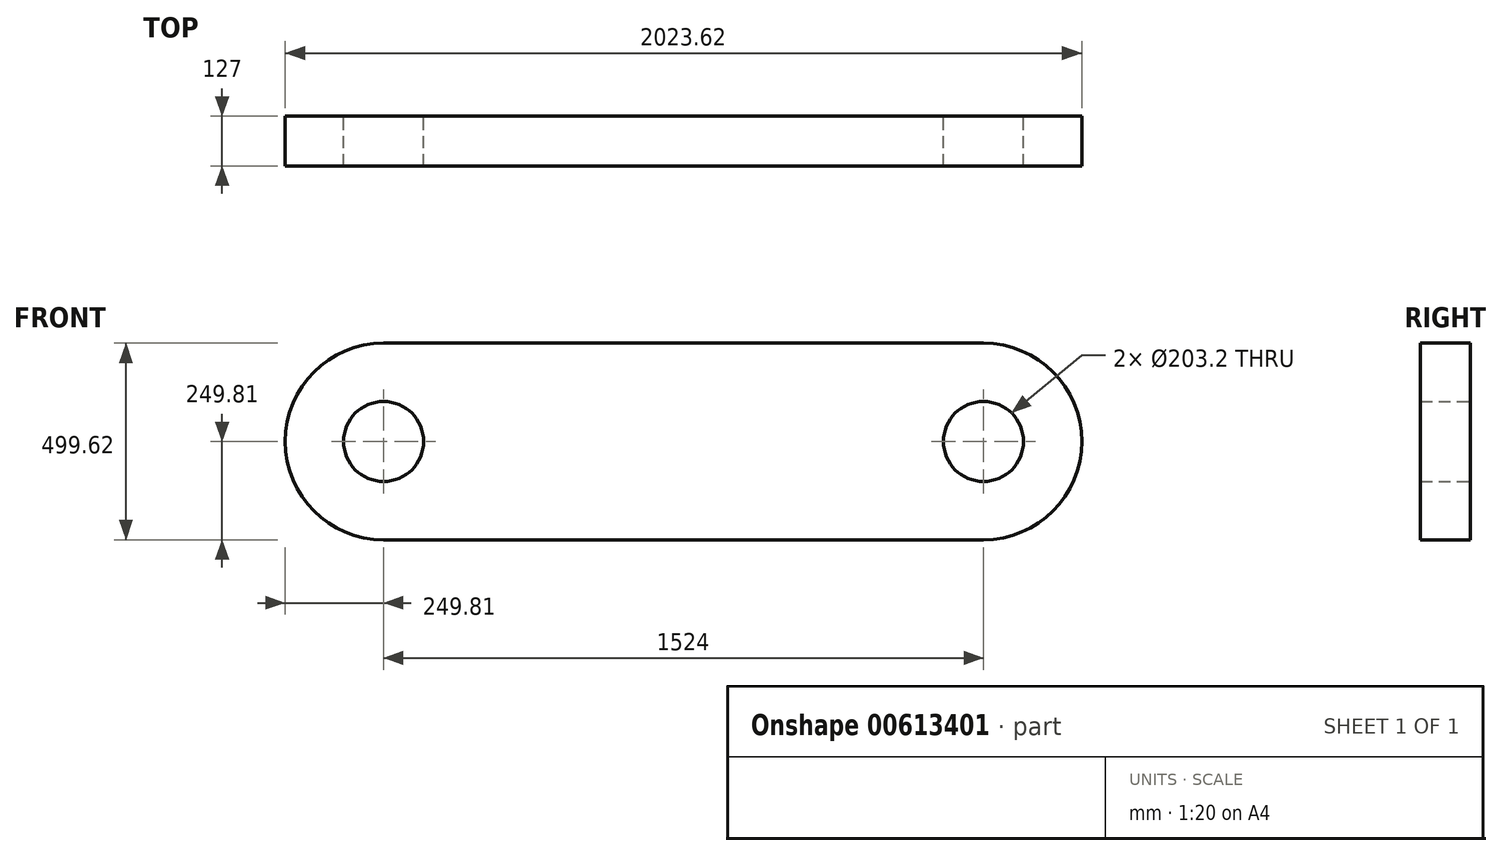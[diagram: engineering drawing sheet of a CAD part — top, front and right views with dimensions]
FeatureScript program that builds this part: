
annotation { "Feature Type Name" : "Feature", "Feature Type Description" : "" }
export const myFeature = defineFeature(function(context is Context, id is Id, definition is map)
    precondition{}
    {
        {
            var Q0;
            Q0=qCreatedBy(makeId("Front.planeOp"),FACE);
            var sketch = newSketch(context, id + "F0", { "sketchPlane" : qUnion([Q0])});
            skLineSegment(sketch, "E0", {"start": v(-762, 0) * mm, "end": v(762, 0) * mm});
            skCircle(sketch, "E1", {"center": v(-762, 0) * mm, "radius": 249.8 * mm});
            skCircle(sketch, "E2", {"center": v(762, 0) * mm, "radius": 249.8 * mm});
            skLineSegment(sketch, "E3", {"start": v(-762, 249.8) * mm, "end": v(762, 249.8) * mm});
            skCircle(sketch, "E4", {"center": v(-762, 0) * mm, "radius": 101.6 * mm});
            skCircle(sketch, "E5", {"center": v(762, 0) * mm, "radius": 101.6 * mm});
            skLineSegment(sketch, "E6", {"start": v(762, -249.8) * mm, "end": v(-762, -249.8) * mm});
            skSolve(sketch);
        }
        {
            var Q0;
            Q0=makeQuery(id+"F0.imprint","IMPRINT",FACE,{"disambiguationData":[TD([[makeQuery(id+"F0.imprint","IMPRINT",EDGE,{"derivedFrom":sQuery(id+"F0.wireOp",EDGE,"E4")}),-1.0]])]});
            var Q1;
            {var subQ5=sQuery(id+"F0.wireOp",EDGE,"E3");Q1=makeQuery(id+"F0.imprint","IMPRINT",FACE,{"disambiguationData":[TD([[makeQuery(id+"F0.imprint","IMPRINT",EDGE,{"derivedFrom":subQ5}),-1.0]])]});}
            var Q2;
            {var subQ5=sQuery(id+"F0.wireOp",EDGE,"E6");Q2=makeQuery(id+"F0.imprint","IMPRINT",FACE,{"disambiguationData":[TD([[makeQuery(id+"F0.imprint","IMPRINT",EDGE,{"derivedFrom":subQ5}),-1.0]])]});}
            var Q3;
            Q3=makeQuery(id+"F0.imprint","IMPRINT",FACE,{"disambiguationData":[TD([[makeQuery(id+"F0.imprint","IMPRINT",EDGE,{"derivedFrom":sQuery(id+"F0.wireOp",EDGE,"E5")}),-1.0]])]});
            extrude(context, id + "F1", {"entities" : qUnion([Q0, Q1, Q2, Q3]), "depth" : 127 * mm, "offsetDistance" : 25.4 * mm});
        }
    });
